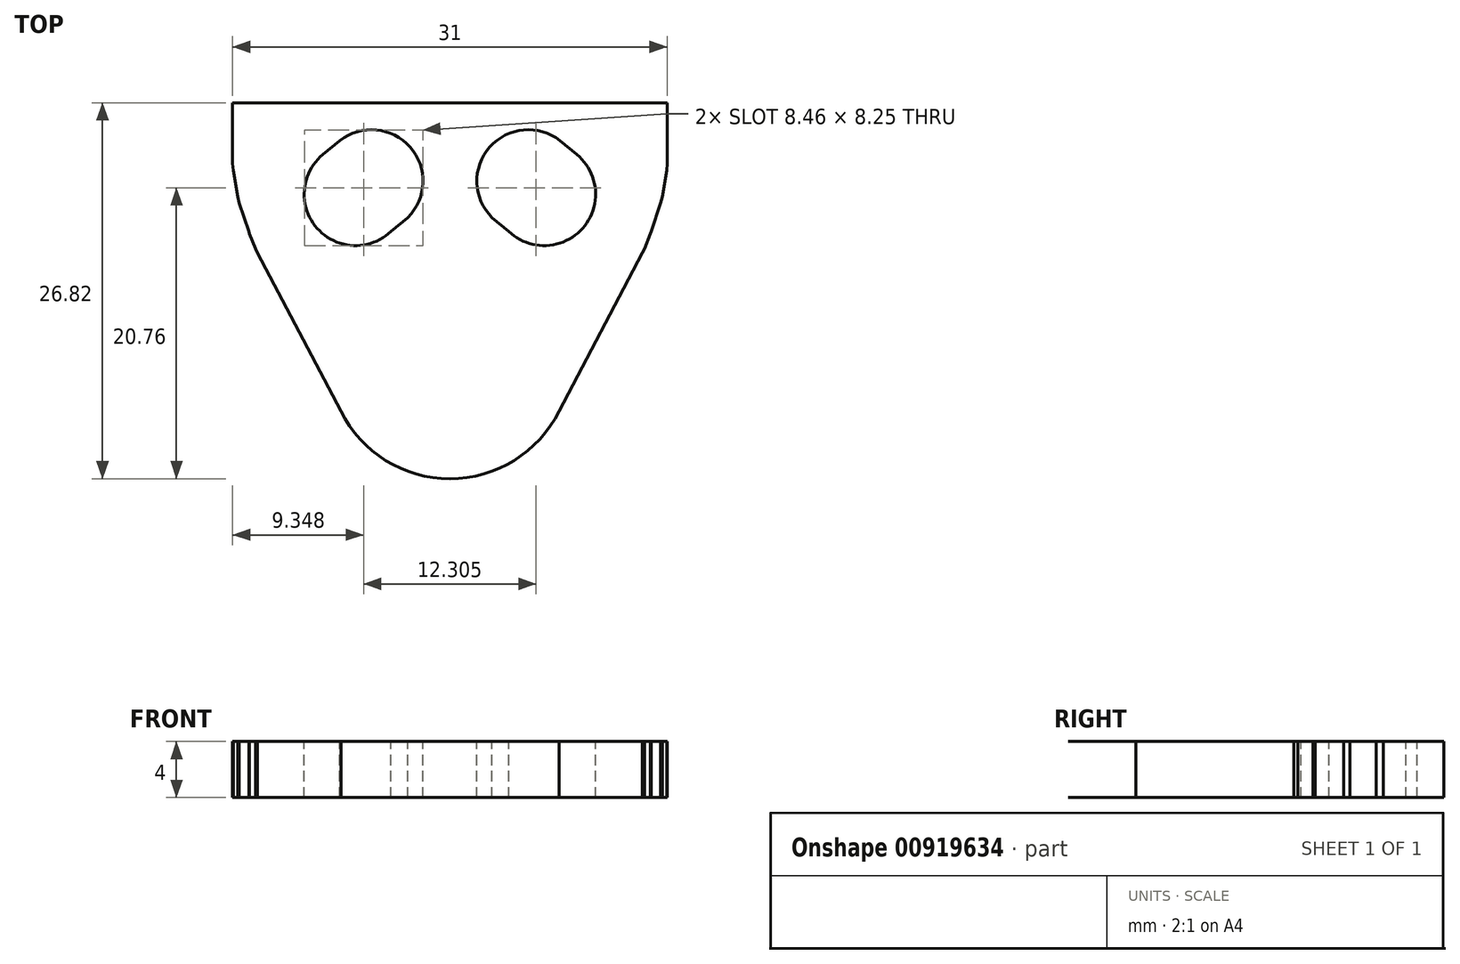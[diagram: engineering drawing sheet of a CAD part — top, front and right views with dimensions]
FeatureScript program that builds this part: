
annotation { "Feature Type Name" : "Feature", "Feature Type Description" : "" }
export const myFeature = defineFeature(function(context is Context, id is Id, definition is map)
    precondition{}
    {
        {
            var Q0;
            Q0=qCreatedBy(makeId("Top.planeOp"),FACE);
            var sketch = newSketch(context, id + "F0", { "sketchPlane" : qUnion([Q0])});
            skLineSegment(sketch, "E0.bottom", {"start": v(0, 0) * mm, "end": v(-12.5, 0) * mm});
            skPoint(sketch, "E0.middle", {"position": v(0, 0) * mm});
            skLineSegment(sketch, "E1", {"start": v(0, 0) * mm, "end": v(0, -23.74) * mm});
            skArc(sketch, "E2", {"start": v(-4.5, -6.58) * mm, "mid": v(-4.5, -4.58) * mm, "end": v(-6.49, -4.41) * mm});
            skArc(sketch, "E3", {"start": v(-7.67, -5.38) * mm, "mid": v(-7.82, -7.53) * mm, "end": v(-5.67, -7.55) * mm});
            skLineSegment(sketch, "E4", {"start": v(-6.49, -4.41) * mm, "end": v(-7.67, -5.38) * mm});
            skLineSegment(sketch, "E5", {"start": v(-5.67, -7.55) * mm, "end": v(-4.5, -6.58) * mm});
            skLineSegment(sketch, "E6.0", {"start": v(-15.5, 0) * mm, "end": v(-15.5, -4.33) * mm});
            skLineSegment(sketch, "E7.0", {"start": v(-15.46, -4.83) * mm, "end": v(-15.14, -6.7) * mm});
            skLineSegment(sketch, "E8.0", {"start": v(-15.03, -7.15) * mm, "end": v(-14.35, -9.19) * mm});
            skLineSegment(sketch, "E9.0", {"start": v(-14.3, -9.34) * mm, "end": v(-13.87, -10.42) * mm});
            skLineSegment(sketch, "E10.0", {"start": v(-13.73, -10.71) * mm, "end": v(-7.78, -22) * mm});
            skArc(sketch, "E11.0", {"start": v(-7.78, -22) * mm, "mid": v(-4.58, -25.52) * mm, "end": v(0, -26.82) * mm});
            skLineSegment(sketch, "E12", {"start": v(-15.5, -4.33) * mm, "end": v(-15.46, -4.83) * mm});
            skLineSegment(sketch, "E13", {"start": v(-15.14, -6.7) * mm, "end": v(-15.03, -7.15) * mm});
            skLineSegment(sketch, "E14", {"start": v(-14.35, -9.19) * mm, "end": v(-14.3, -9.34) * mm});
            skLineSegment(sketch, "E15", {"start": v(-13.87, -10.42) * mm, "end": v(-13.73, -10.71) * mm});
            skLineSegment(sketch, "E16", {"start": v(-7.78, -22) * mm, "end": v(-7.78, -22) * mm});
            skLineSegment(sketch, "E17", {"start": v(0, -23.74) * mm, "end": v(0, -26.82) * mm});
            skLineSegment(sketch, "E18", {"start": v(-15.5, 0) * mm, "end": v(-12.5, 0) * mm});
            skLineSegment(sketch, "E19.0", {"start": v(-7.85, -2.7) * mm, "end": v(-9.06, -3.7) * mm});
            skArc(sketch, "E19.1", {"start": v(-3, -8.19) * mm, "mid": v(-2.84, -3.16) * mm, "end": v(-7.85, -2.7) * mm});
            skLineSegment(sketch, "E19.2", {"start": v(-4.2, -9.18) * mm, "end": v(-3, -8.19) * mm});
            skArc(sketch, "E19.3", {"start": v(-9.06, -3.7) * mm, "mid": v(-9.47, -8.95) * mm, "end": v(-4.2, -9.18) * mm});
            skSolve(sketch);
        }
        {
            var Q0;
            Q0=makeQuery(id+"F0.imprint","IMPRINT",FACE,{"disambiguationData":[TD([[makeQuery(id+"F0.imprint","IMPRINT",EDGE,{"derivedFrom":sQuery(id+"F0.wireOp",EDGE,"E0.bottom")}),1.0]])]});
            extrude(context, id + "F1", {"entities" : qUnion([Q0]), "oppositeDirection" : true, "depth" : 4 * mm, "offsetDistance" : 25 * mm});
        }
        {
            var Q0;
            Q0=makeQuery(id+"F1.opExtrude","SWEPT_BODY",BODY,{"disambiguationData":[OSD([sQuery(id+"F0.wireOp",EDGE,"Wc3MDDFG-ihRC-nruT-XZi2-AqeFWlMTdI7O"),sQuery(id+"F0.wireOp",EDGE,"E0.bottom"),sQuery(id+"F0.wireOp",EDGE,"E0.right"),sQuery(id+"F0.wireOp",EDGE,"5d4e1d1e-83f1-4f70-bb5c-0ff6b9ec7679"),sQuery(id+"F0.wireOp",EDGE,"E1"),sQuery(id+"F0.wireOp",EDGE,"E2"),sQuery(id+"F0.wireOp",EDGE,"E3"),sQuery(id+"F0.wireOp",EDGE,"E4"),sQuery(id+"F0.wireOp",EDGE,"E5")])]});
            var Q1;
            Q1=qCreatedBy(makeId("Right.planeOp"),FACE);
            mirror(context, id + "F2", {"operationType" : NewBodyOperationType.ADD, "entities" : qUnion([Q0]), "mirrorPlane" : qUnion([Q1])});
        }
    });
